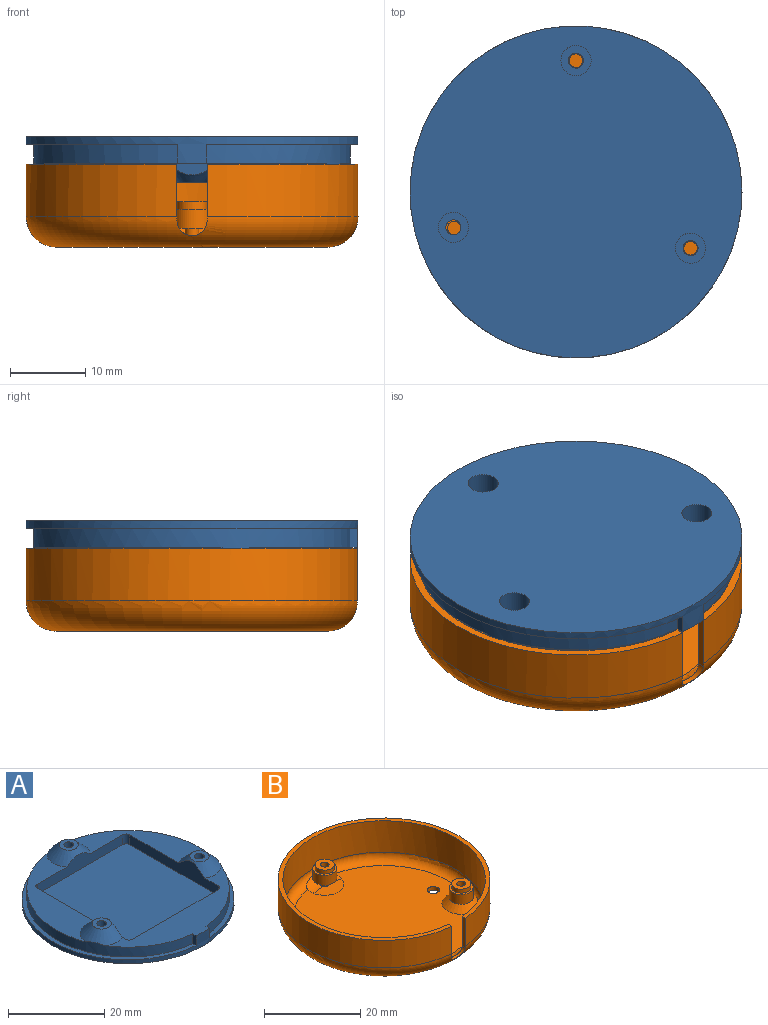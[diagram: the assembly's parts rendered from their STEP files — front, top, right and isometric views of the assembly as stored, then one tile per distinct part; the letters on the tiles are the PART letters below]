
ASSEMBLY  parts=2 mates=1
PART A: 33 faces, bbox 44.1x44.1x6 mm
  f0: plane 24.67x18.09mm, normal (0,0,1), area 125.7mm2, adj f6,f8,f9,f15,f30,f31
  f1: plane 28.23x18.09mm, normal (0,0,1), area 161.2mm2, adj f6,f13,f14,f15,f30,f32
  f2: cylinder r=2mm len=4mm, axis (0,0,-1), area 42.7mm2, adj f18,f29
  f3: cylinder r=2mm len=4mm, axis (0,0,-1), area 42.7mm2, adj f18,f26
  f4: cylinder r=2mm len=4mm, axis (0,0,-1), area 42.7mm2, adj f18,f23
  f5: plane 2.5x1mm, normal (1,0,0), area 2.5mm2, adj f6,f16,f17,f19
  f6: cylinder r=21.05mm len=42.1mm, axis (0,0,-1), area 326.6mm2, adj f0,f1,f5,f7,f17,f19,f30,f31
  f7: plane 2.5x1mm, normal (-1,0,0), area 2.5mm2, adj f6,f16,f17,f19
  f8: cylinder r=1mm len=2.5mm, axis (0,0,-1), area 3.9mm2, adj f0,f9,f15,f20
  f9: plane 26x4.72mm, normal (-1,0,0), area 75.7mm2, adj f0,f8,f10,f17,f20,f31
  f10: cylinder r=1mm len=2.5mm, axis (0,0,-1), area 3.9mm2, adj f9,f11,f17,f20
  f11: plane 25.2x2.5mm, normal (0,1,0), area 63mm2, adj f10,f12,f17,f20
  f12: cylinder r=1mm len=2.5mm, axis (0,0,-1), area 3.9mm2, adj f11,f13,f17,f20
  f13: plane 26x4.99mm, normal (1,0,0), area 77.3mm2, adj f1,f12,f14,f17,f20,f32
  f14: cylinder r=1mm len=2.5mm, axis (0,0,-1), area 3.9mm2, adj f1,f13,f15,f20
  f15: plane 25.2x4.05mm, normal (0,-1,0), area 69.7mm2, adj f0,f1,f8,f14,f20,f30
  f16: cylinder r=22.05mm len=44.1mm, axis (0,0,-1), area 148.3mm2, adj f5,f7,f17,f18,f19
  f17: plane 37.44x14.24mm, normal (0,0,1), area 197.2mm2, adj f5,f6,f7,f9,f10,f11,f12,f13
  f18: plane 44.1x44.1mm, normal (0,0,-1), area 1489.8mm2, adj f2,f3,f4,f16
  f19: plane 44.1x44.01mm, normal (0,0,1), area 131.5mm2, adj f5,f6,f7,f16
  f20: plane 28x27.2mm, normal (0,0,1), area 760.7mm2, adj f8,f9,f10,f11,f12,f13,f14,f15
  f21: cylinder r=1mm len=2.6mm, axis (0,0,-1), area 16.3mm2, adj f22,f23
  f22: plane 4x4mm, normal (0,0,1), area 9.4mm2, adj f21,f31
  f23: plane 4x4mm, normal (0,0,-1), area 9.4mm2, adj f4,f21
  f24: cylinder r=1mm len=2.6mm, axis (0,0,-1), area 16.3mm2, adj f25,f26
  f25: plane 4x4mm, normal (0,0,1), area 9.4mm2, adj f24,f30
  f26: plane 4x4mm, normal (0,0,-1), area 9.4mm2, adj f3,f24
  f27: cylinder r=1mm len=2.6mm, axis (0,0,-1), area 16.3mm2, adj f28,f29
  f28: plane 4x4mm, normal (0,0,1), area 9.4mm2, adj f27,f32
  f29: plane 4x4mm, normal (0,0,-1), area 9.4mm2, adj f2,f27
  f30: cone r=2mm half-angle=45deg, axis (0,0,-1), area 56.7mm2, adj f0,f1,f6,f15,f25
  f31: cone r=2mm half-angle=45deg, axis (0,0,-1), area 53.4mm2, adj f0,f6,f9,f17,f22
  f32: cone r=2mm half-angle=45deg, axis (0,0,-1), area 50.4mm2, adj f1,f6,f13,f17,f28
PART B: 33 faces, bbox 47.7x47.7x11 mm
  f0: cylinder r=0.9mm len=5mm, axis (0,0,-1), area 28.3mm2, adj f2,f24
  f1: cylinder r=2mm len=4mm, axis (0,0,-1), area 12.6mm2, adj f2,f5
  f2: plane 4x4mm, normal (0,0,1), area 10mm2, adj f0,f1
  f3: plane 36.1x36.1mm, normal (0,0,-1), area 1013.7mm2, adj f19,f20,f32
  f4: cylinder r=2.5mm len=5mm, axis (0,0,-1), area 39.3mm2, adj f5,f29
  f5: plane 5x5mm, normal (0,0,1), area 7.1mm2, adj f1,f4
  f6: cylinder r=0.9mm len=5mm, axis (0,0,-1), area 28.3mm2, adj f8,f23
  f7: cylinder r=2mm len=4mm, axis (0,0,-1), area 12.6mm2, adj f8,f10
  f8: plane 4x4mm, normal (0,0,1), area 10mm2, adj f6,f7
  f9: cylinder r=2.5mm len=5mm, axis (0,0,-1), area 39.3mm2, adj f10,f30
  f10: plane 5x5mm, normal (0,0,1), area 7.1mm2, adj f7,f9
  f11: cylinder r=0.9mm len=5mm, axis (0,0,-1), area 28.3mm2, adj f13,f22
  f12: cylinder r=2mm len=4mm, axis (0,0,-1), area 12.6mm2, adj f13,f15
  f13: plane 4x4mm, normal (0,0,1), area 10mm2, adj f11,f12
  f14: cylinder r=2.5mm len=5mm, axis (0,0,-1), area 39.3mm2, adj f15,f28
  f15: plane 5x5mm, normal (0,0,1), area 7.1mm2, adj f12,f14
  f16: cylinder r=21.05mm len=42.1mm, axis (0,0,-1), area 1026.1mm2, adj f18,f25,f26,f27,f31
  f17: cylinder r=22.05mm len=44.1mm, axis (0,0,-1), area 941.8mm2, adj f18,f26,f27,f32
  f18: plane 44.1x44.01mm, normal (0,0,1), area 131.4mm2, adj f16,f17,f26,f27
  f19: cylinder r=1.25mm len=2.5mm, axis (0,0,-1), area 8mm2, adj f3,f21,f30
  f20: cylinder r=1.25mm len=2.5mm, axis (0,0,-1), area 7.9mm2, adj f3,f21
  f21: plane 38.1x37.72mm, normal (0,0,1), area 1012.4mm2, adj f19,f20,f28,f29,f30,f31
  f22: plane 1.8x1.8mm, normal (0,0,1), area 2.5mm2, adj f11
  f23: plane 1.8x1.8mm, normal (0,0,1), area 2.5mm2, adj f6
  f24: plane 1.8x1.8mm, normal (0,0,1), area 2.5mm2, adj f0
  f25: cylinder r=2mm len=4mm, axis (0,1,0), area 5mm2, adj f16,f26,f27,f31,f32
  f26: plane 7.5x1.01mm, normal (-1,0,0), area 7.5mm2, adj f16,f17,f18,f25,f32
  f27: plane 7.5x1.01mm, normal (1,0,0), area 7.5mm2, adj f16,f17,f18,f25,f32
  f28: cone r=2.5mm half-angle=45deg, axis (0,0,-1), area 39.7mm2, adj f14,f21,f31
  f29: cone r=2.5mm half-angle=45deg, axis (0,0,-1), area 37.3mm2, adj f4,f21,f31
  f30: cone r=2.5mm half-angle=45deg, axis (0,0,-1), area 39.8mm2, adj f9,f19,f21,f31
  f31: torus R=19.05mm, axis (0,0,1), area 370.8mm2, adj f16,f21,f25,f28,f29,f30
  f32: torus R=18.05mm, axis (0,0,1), area 804.3mm2, adj f3,f17,f25,f26,f27
PLACE A rot(axis=(0,-1,0),180deg) t=(-3.11,9.08,-1.39)mm
PLACE B t=(-3.11,9.08,-16.03)mm
MATE slider B.f16 <-> A.f6  axis (0,0,1) through (-3.11,9.08,-5.03)mm
